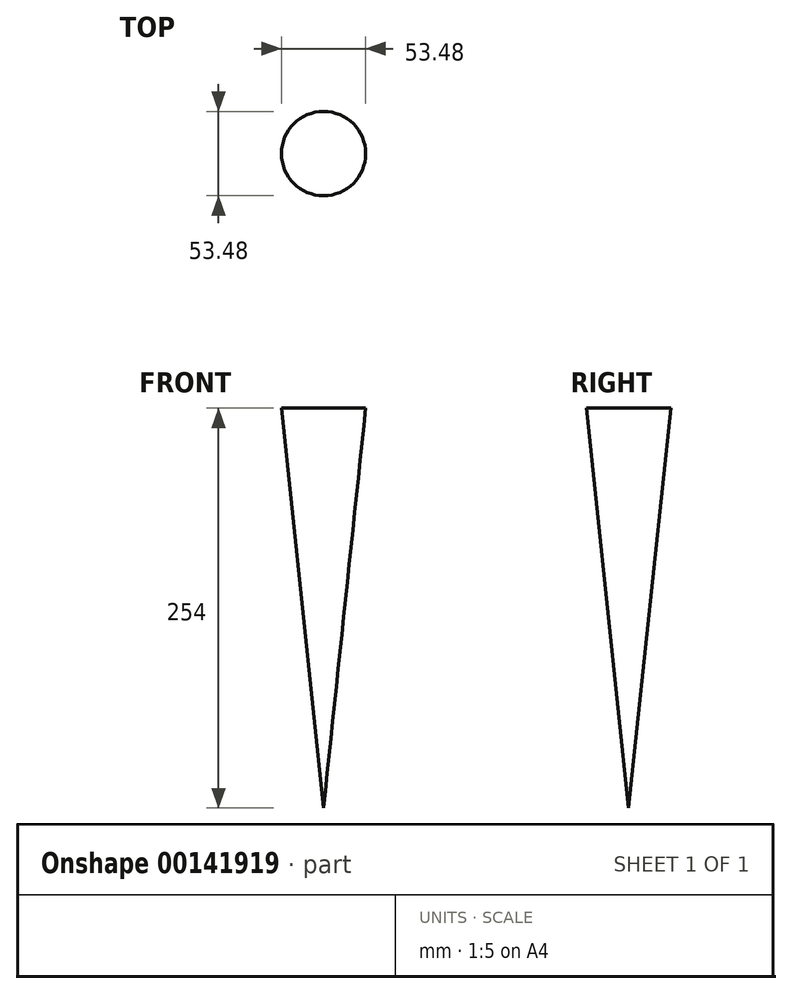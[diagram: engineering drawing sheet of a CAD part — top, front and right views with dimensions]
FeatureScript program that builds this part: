
annotation { "Feature Type Name" : "Feature", "Feature Type Description" : "" }
export const myFeature = defineFeature(function(context is Context, id is Id, definition is map)
    precondition{}
    {
        {
            var Q0;
            Q0=qCreatedBy(makeId("Front.planeOp"),FACE);
            var sketch = newSketch(context, id + "F0", { "sketchPlane" : qUnion([Q0])});
            skLineSegment(sketch, "E0", {"start": v(0, 0) * mm, "end": v(0, -254) * mm});
            skLineSegment(sketch, "E1", {"start": v(24.06, 0) * mm, "end": v(-26.74, 0) * mm});
            skLineSegment(sketch, "E2", {"start": v(0, -254) * mm, "end": v(24.06, 0) * mm});
            skLineSegment(sketch, "E3", {"start": v(0, -254) * mm, "end": v(-26.74, 0) * mm});
            skSolve(sketch);
        }
        {
            var Q0;
            {var subQ0=sQuery(id+"F0.wireOp",EDGE,"E0");Q0=makeQuery(id+"F0.imprint","IMPRINT",FACE,{"disambiguationData":[TD([[makeQuery(id+"F0.imprint","IMPRINT",EDGE,{"derivedFrom":subQ0}),-1.0]])]});}
            var Q1;
            Q1=sQuery(id+"F0.wireOp",EDGE,"E0");
            revolve(context, id + "F1", {"entities" : qUnion([Q0]), "axis" : qUnion([Q1]), "revolveType" : RevolveType.FULL});
        }
    });
